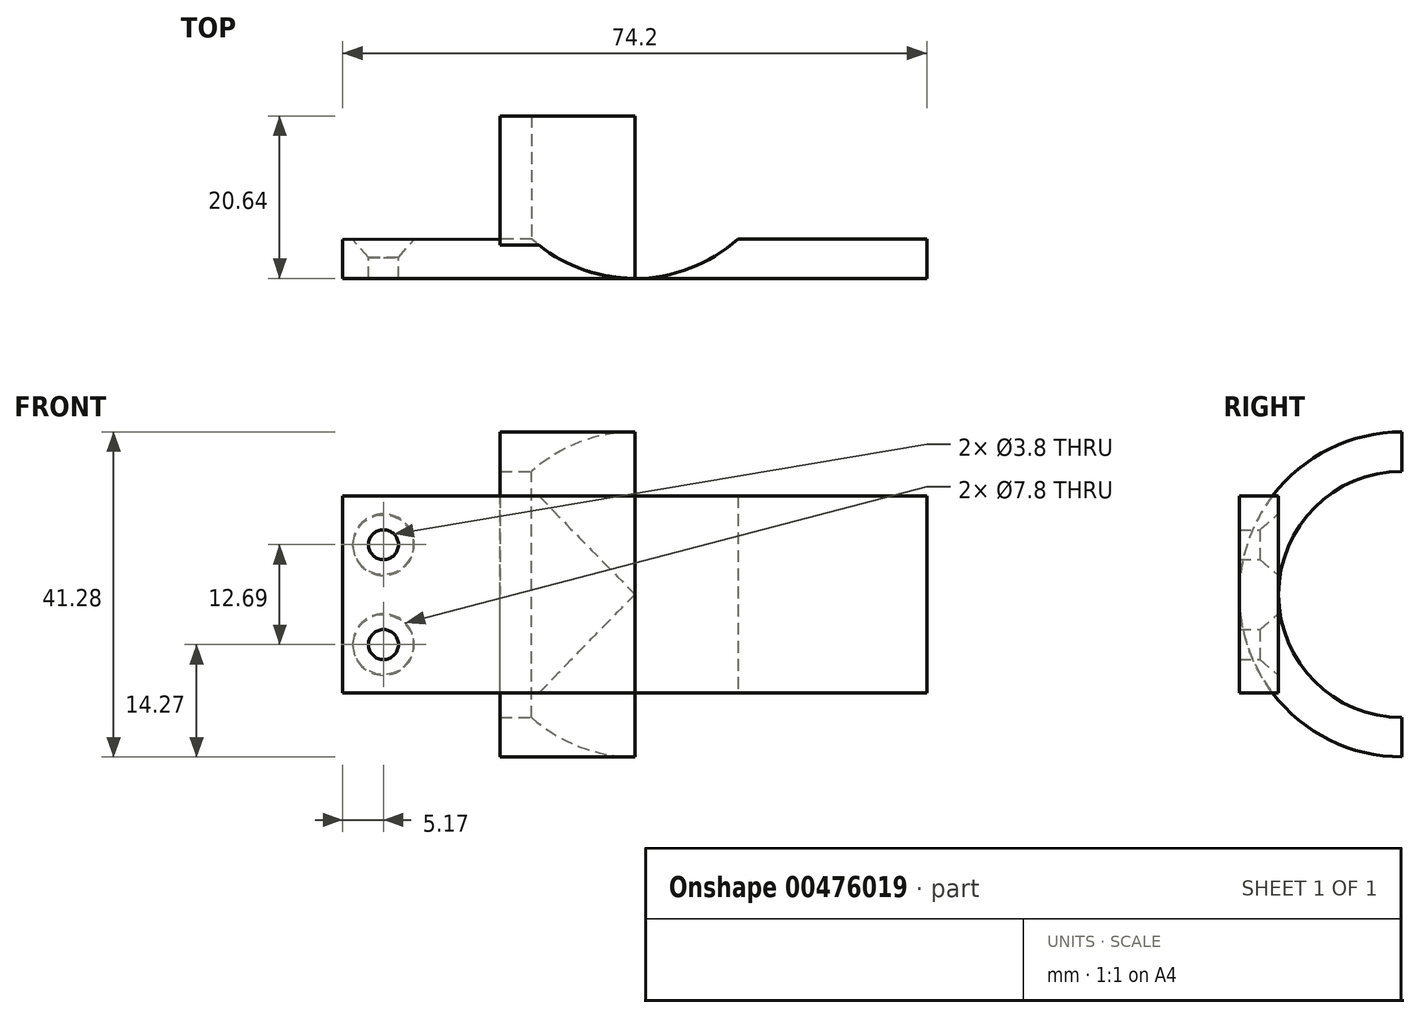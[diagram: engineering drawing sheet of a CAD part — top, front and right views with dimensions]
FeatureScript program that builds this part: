
annotation { "Feature Type Name" : "Feature", "Feature Type Description" : "" }
export const myFeature = defineFeature(function(context is Context, id is Id, definition is map)
    precondition{}
    {
        {
            var Q0;
            Q0=qCreatedBy(makeId("Top.planeOp"),FACE);
            var sketch = newSketch(context, id + "F0", { "sketchPlane" : qUnion([Q0])});
            skLineSegment(sketch, "E0", {"start": v(-14.57, 0) * mm, "end": v(14.64, 0) * mm, "construction": true});
            skArc(sketch, "E1", {"start": v(14.64, 0) * mm, "mid": v(0, -14.64) * mm, "end": v(-14.64, 0) * mm});
            skArc(sketch, "E2.0", {"start": v(19.64, 0) * mm, "mid": v(0, -19.64) * mm, "end": v(-19.64, 0) * mm});
            skLineSegment(sketch, "E3", {"start": v(-34.14, 1) * mm, "end": v(46.26, 1) * mm, "construction": true});
            skLineSegment(sketch, "E4", {"start": v(-19.64, 0) * mm, "end": v(-14.57, 0) * mm});
            skLineSegment(sketch, "E5", {"start": v(14.64, 0) * mm, "end": v(19.64, 0) * mm});
            skPoint(sketch, "E6", {"position": v(0, -14.64) * mm});
            skLineSegment(sketch, "E7", {"start": v(0, -14.64) * mm, "end": v(0, 5.46) * mm, "construction": true});
            skPoint(sketch, "E8", {"position": v(0, 1) * mm});
            skPoint(sketch, "E9.firstSnap0", {"position": v(-17.1, 0) * mm});
            skLineSegment(sketch, "E9.bottom", {"start": v(-17.1, -14.64) * mm, "end": v(17.1, -14.64) * mm});
            skLineSegment(sketch, "E9.top", {"start": v(-17.1, -19.64) * mm, "end": v(17.1, -19.64) * mm});
            skLineSegment(sketch, "E9.left", {"start": v(-17.1, -14.64) * mm, "end": v(-17.1, -19.64) * mm});
            skLineSegment(sketch, "E9.right", {"start": v(17.1, -14.64) * mm, "end": v(17.1, -19.64) * mm});
            skLineSegment(sketch, "E10", {"start": v(-17.1, -19.64) * mm, "end": v(-37.1, -19.64) * mm});
            skLineSegment(sketch, "E11", {"start": v(-37.1, -19.64) * mm, "end": v(-37.1, -14.7) * mm});
            skLineSegment(sketch, "E12", {"start": v(-37.1, -14.7) * mm, "end": v(-17.1, -14.64) * mm});
            skLineSegment(sketch, "E13", {"start": v(17.1, -19.64) * mm, "end": v(37.1, -19.64) * mm});
            skLineSegment(sketch, "E14", {"start": v(37.1, -19.64) * mm, "end": v(37.1, -14.64) * mm});
            skLineSegment(sketch, "E15", {"start": v(37.1, -14.64) * mm, "end": v(17.1, -14.64) * mm});
            skSolve(sketch);
        }
        {
            var Q0;
            {var subQ0=sQuery(id+"F0.wireOp",EDGE,"E1");Q0=makeQuery(id+"F0.imprint","IMPRINT",FACE,{"disambiguationData":[TD([[makeQuery(id+"F0.imprint","IMPRINT",EDGE,{"derivedFrom":subQ0}),1.0]])]});}
            var Q1;
            {var subQ0=sQuery(id+"F0.wireOp",EDGE,"E9.bottom");var subQ1=sQuery(id+"F0.wireOp",EDGE,"E2.0");var subQ2=makeQuery(id+"F0.imprint","INTERSECT",VERTEX,{"disambiguationData":[OD(0.0)],"derivedFrom":[subQ1,subQ0]});Q1=makeQuery(id+"F0.imprint","IMPRINT",FACE,{"disambiguationData":[TD([[makeQuery(id+"F0.imprint","IMPRINT",EDGE,{"disambiguationData":[TD([[subQ2,-1.0]])],"derivedFrom":subQ1}),-1.0]])]});}
            var Q2;
            Q2=sQuery(id+"F0.wireOp",EDGE,"E3");
            revolve(context, id + "F1", {"entities" : qUnion([Q0, Q1]), "axis" : qUnion([Q2]), "revolveType" : RevolveType.SYMMETRIC, "angle" : 180 * degree});
        }
        {
            var Q0;
            {var subQ5=sQuery(id+"F0.wireOp",EDGE,"E9.right");Q0=makeQuery(id+"F0.imprint","IMPRINT",FACE,{"disambiguationData":[TD([[makeQuery(id+"F0.imprint","IMPRINT",EDGE,{"derivedFrom":subQ5}),-1.0]])]});}
            var Q1;
            {var subQ5=sQuery(id+"F0.wireOp",EDGE,"E9.left");Q1=makeQuery(id+"F0.imprint","IMPRINT",FACE,{"disambiguationData":[TD([[makeQuery(id+"F0.imprint","IMPRINT",EDGE,{"derivedFrom":subQ5}),1.0]])]});}
            var Q2;
            {var subQ0=sQuery(id+"F0.wireOp",EDGE,"E9.bottom");var subQ1=sQuery(id+"F0.wireOp",EDGE,"E2.0");var subQ2=makeQuery(id+"F0.imprint","INTERSECT",VERTEX,{"disambiguationData":[OD(0.0)],"derivedFrom":[subQ1,subQ0]});Q2=makeQuery(id+"F0.imprint","IMPRINT",FACE,{"disambiguationData":[TD([[makeQuery(id+"F0.imprint","IMPRINT",EDGE,{"disambiguationData":[TD([[subQ2,-1.0]])],"derivedFrom":subQ1}),-1.0]])]});}
            extrude(context, id + "F2", {"entities" : qUnion([Q0, Q1, Q2]), "operationType" : NewBodyOperationType.ADD, "endBound" : BoundingType.SYMMETRIC, "depth" : 25 * mm});
        }
        {
            var Q0;
            Q0=makeQuery(id+"F0.imprint","IMPRINT",FACE,{"disambiguationData":[TD([[makeQuery(id+"F0.imprint","IMPRINT",EDGE,{"derivedFrom":sQuery(id+"F0.wireOp",EDGE,"E9.right")}),1.0]])]});
            var Q1;
            Q1=makeQuery(id+"F0.imprint","IMPRINT",FACE,{"disambiguationData":[TD([[makeQuery(id+"F0.imprint","IMPRINT",EDGE,{"derivedFrom":sQuery(id+"F0.wireOp",EDGE,"E9.left")}),-1.0]])]});
            extrude(context, id + "F3", {"entities" : qUnion([Q0, Q1]), "operationType" : NewBodyOperationType.ADD, "depth" : 12.5 * mm});
        }
        {
            var Q0;
            Q0=makeQuery(id+"F0.imprint","IMPRINT",FACE,{"disambiguationData":[TD([[makeQuery(id+"F0.imprint","IMPRINT",EDGE,{"derivedFrom":sQuery(id+"F0.wireOp",EDGE,"E9.right")}),1.0]])]});
            var Q1;
            Q1=makeQuery(id+"F0.imprint","IMPRINT",FACE,{"disambiguationData":[TD([[makeQuery(id+"F0.imprint","IMPRINT",EDGE,{"derivedFrom":sQuery(id+"F0.wireOp",EDGE,"E9.left")}),-1.0]])]});
            extrude(context, id + "F4", {"entities" : qUnion([Q0, Q1]), "operationType" : NewBodyOperationType.ADD, "oppositeDirection" : true, "depth" : 12.5 * mm});
        }
        {
            var Q0;
            Q0=qCreatedBy(makeId("Front.planeOp"),FACE);
            var sketch = newSketch(context, id + "F5", { "sketchPlane" : qUnion([Q0])});
            skLineSegment(sketch, "E16", {"start": v(19.64, 0) * mm, "end": v(19.64, -12.7) * mm, "construction": true});
            skLineSegment(sketch, "E17", {"start": v(19.64, 0) * mm, "end": v(19.64, 13.41) * mm, "construction": true});
            skLineSegment(sketch, "E18", {"start": v(19.64, 6.7) * mm, "end": v(37.05, 6.7) * mm, "construction": true});
            skLineSegment(sketch, "E19", {"start": v(19.64, -6.35) * mm, "end": v(37.47, -6.35) * mm, "construction": true});
            skLineSegment(sketch, "E20", {"start": v(-26.93, 12.85) * mm, "end": v(-26.93, -12.42) * mm, "construction": true});
            skPoint(sketch, "E21", {"position": v(32.33, 6.7) * mm});
            skPoint(sketch, "E22", {"position": v(32.33, -6.35) * mm});
            skPoint(sketch, "E22.positionSnap0", {"position": v(28.56, -6.35) * mm});
            skLineSegment(sketch, "E23", {"start": v(32.33, 11.2) * mm, "end": v(37.33, 11.2) * mm, "construction": true});
            skLineSegment(sketch, "E24", {"start": v(-36.93, 12.85) * mm, "end": v(-36.93, -12.42) * mm, "construction": true});
            skLineSegment(sketch, "E25", {"start": v(-36.93, 0.21) * mm, "end": v(-26.93, 0.21) * mm, "construction": true});
            skLineSegment(sketch, "E26", {"start": v(-31.93, 0.21) * mm, "end": v(-31.93, 12.43) * mm, "construction": true});
            skLineSegment(sketch, "E27", {"start": v(-31.93, 0.21) * mm, "end": v(-31.93, -12.95) * mm, "construction": true});
            skLineSegment(sketch, "E28", {"start": v(-31.93, 7.92) * mm, "end": v(-36.93, 7.92) * mm, "construction": true});
            skLineSegment(sketch, "E29", {"start": v(37.2, 12.6) * mm, "end": v(37.2, -12.3) * mm, "construction": true});
            skLineSegment(sketch, "E30", {"start": v(32.33, 12.67) * mm, "end": v(32.33, -12.46) * mm, "construction": true});
            skLineSegment(sketch, "E31", {"start": v(-31.93, 6.32) * mm, "end": v(-36.93, 6.32) * mm, "construction": true});
            skLineSegment(sketch, "E32", {"start": v(-31.93, -6.37) * mm, "end": v(-36.93, -6.37) * mm, "construction": true});
            skPoint(sketch, "E33", {"position": v(-31.93, -6.37) * mm});
            skPoint(sketch, "E34", {"position": v(-31.93, 6.32) * mm});
            skSolve(sketch);
        }
        {
            var Q0;
            Q0=sQuery(id+"F5.wireOp",VERTEX,"E21");
            var Q1;
            Q1=sQuery(id+"F5.wireOp",VERTEX,"E22");
            var Q2;
            Q2=sQuery(id+"F5.wireOp",VERTEX,"E34");
            var Q3;
            Q3=sQuery(id+"F5.wireOp",VERTEX,"E33");
            var Q4;
            Q4=makeQuery(id+"F1.opRevolve","SWEPT_BODY",BODY,{"disambiguationData":[OSD([sQuery(id+"F0.wireOp",EDGE,"E1"),sQuery(id+"F0.wireOp",EDGE,"E2.0"),sQuery(id+"F0.wireOp",EDGE,"E4"),sQuery(id+"F0.wireOp",EDGE,"E5")])]});
            hole(context, id + "F6", {"style" : HoleStyle.C_SINK, "endStyle" : HoleEndStyle.BLIND, "oppositeDirection" : true, "standardTappedOrClearance" : lookupTablePath({ "standard" : "ANSI", "fit" : "Normal (ASME)", "size" : "#6", "type" : "Clearance" }), "standardBlindInLast" : lookupTablePath({ "fit" : "Free", "standard" : "ANSI", "size" : "#6", "type" : "Clearance" }), "holeDiameter" : 3.8 * mm, "cSinkDiameter" : 7.8 * mm, "cSinkAngle" : 82 * degree, "holeDepth" : 14.38 * mm, "isTappedThrough" : true, "tappedDepth" : 12 * mm, "tapClearance" : 3, "locations" : qUnion([Q0, Q1, Q2, Q3]), "scope" : qUnion([Q4])});
        }
    });
